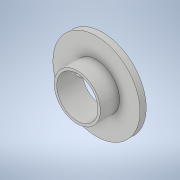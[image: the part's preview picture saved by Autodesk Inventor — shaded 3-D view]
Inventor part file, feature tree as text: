
AUTODESK INVENTOR PART (.ipt)
format: ipt  version: 2021 (Build 250183000, 183)  size: 144,896 bytes
history: native  units: in
note: dims shown in document units (in); Inventor stores cm internally (conversion verified against a paired STEP export)
features: sketch x4, extrude x3, revolve x1
ambient origin geometry x8: Origin, YZ Plane, XZ Plane, XY Plane, X Axis, Y Axis, Z Axis, Center Point
bodies: Solid1 (feature_tree)
feature tree (8):
  revolve  "Revolution1"  [1 undecoded]
  extrude  "Extrusion1"  Depth=0.265in
  extrude  "Extrusion2"  Depth=1.75in
  extrude  "Extrusion3"  Depth=0.188in
  sketch  "Sketch1"  dims[d1=0.98in d2=0.813in]
  sketch  "Sketch2"  dims[d3=0.8705in d4=0.265in]
  sketch  "Sketch3"  dims[d5=90.0deg d6=1.75in]
  sketch  "Sketch4"  dims[d7=1.125in d8=0.0in d10=0.375in d12=0.105in d13=1.0625in d14=0.0in d15=0.188in d16=0.1in d17=0.0in]
note: 1 required parameter value undecoded (feature->parameter linkage not recoverable at this tier; creation-order binding heuristic only, values carry confidence <= 0.55)
